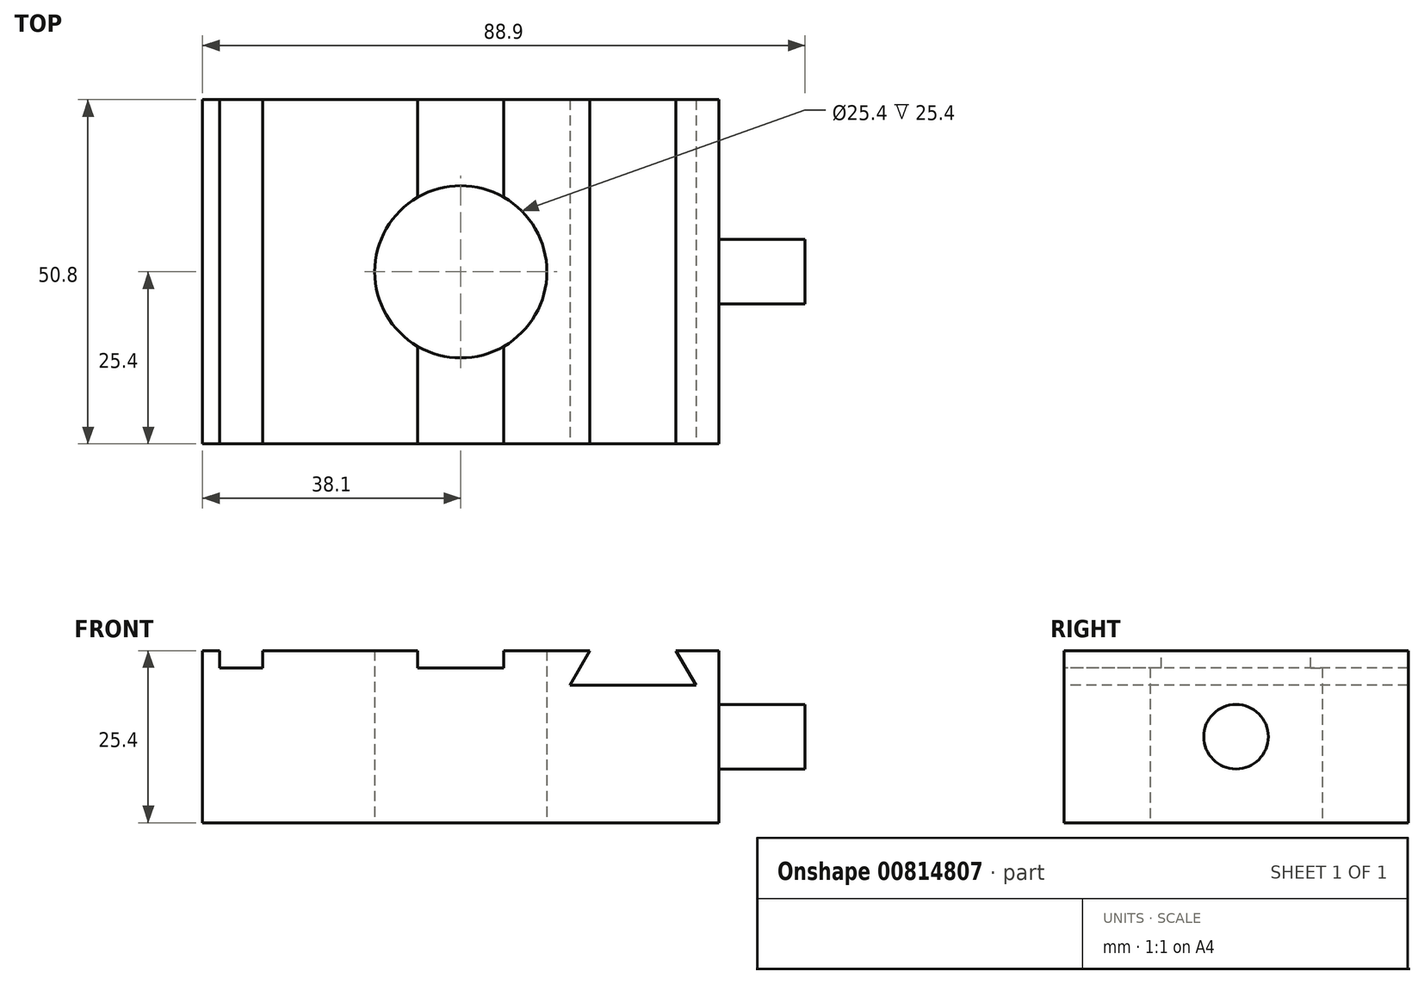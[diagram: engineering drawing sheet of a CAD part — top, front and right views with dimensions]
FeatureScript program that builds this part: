
annotation { "Feature Type Name" : "Feature", "Feature Type Description" : "" }
export const myFeature = defineFeature(function(context is Context, id is Id, definition is map)
    precondition{}
    {
        {
            var Q0;
            Q0=qCreatedBy(makeId("Top.planeOp"),FACE);
            var sketch = newSketch(context, id + "F0", { "sketchPlane" : qUnion([Q0])});
            skLineSegment(sketch, "E0.bottom", {"start": v(-38.1, 25.4) * mm, "end": v(38.1, 25.4) * mm});
            skLineSegment(sketch, "E0.top", {"start": v(-38.1, -25.4) * mm, "end": v(38.1, -25.4) * mm});
            skLineSegment(sketch, "E0.left", {"start": v(-38.1, 25.4) * mm, "end": v(-38.1, -25.4) * mm});
            skLineSegment(sketch, "E0.right", {"start": v(38.1, 25.4) * mm, "end": v(38.1, -25.4) * mm});
            skPoint(sketch, "E0.middle", {"position": v(0, 0) * mm});
            skCircle(sketch, "E1", {"center": v(0, 0) * mm, "radius": 12.7 * mm});
            skSolve(sketch);
        }
        {
            var Q0;
            Q0=makeQuery(id+"F0.imprint","IMPRINT",FACE,{"disambiguationData":[TD([[makeQuery(id+"F0.imprint","IMPRINT",EDGE,{"derivedFrom":sQuery(id+"F0.wireOp",EDGE,"E0.bottom")}),-1.0]])]});
            extrude(context, id + "F1", {"entities" : qUnion([Q0]), "depth" : 25.4 * mm, "offsetDistance" : 25 * mm});
        }
        {
            var Q0;
            Q0=makeQuery(id+"F1.opExtrude","CAP_FACE",FACE,{"disambiguationData":[OSD([sQuery(id+"F0.wireOp",EDGE,"E0.bottom"),sQuery(id+"F0.wireOp",EDGE,"E0.top"),sQuery(id+"F0.wireOp",EDGE,"E0.left"),sQuery(id+"F0.wireOp",EDGE,"E0.right"),sQuery(id+"F0.wireOp",EDGE,"E1")])],"isStart":false});
            var sketch = newSketch(context, id + "F2", { "sketchPlane" : qUnion([Q0])});
            skLineSegment(sketch, "E2.bottom", {"start": v(-35.56, 25.4) * mm, "end": v(-29.21, 25.4) * mm});
            skLineSegment(sketch, "E2.top", {"start": v(-35.56, -25.4) * mm, "end": v(-29.21, -25.4) * mm});
            skLineSegment(sketch, "E2.left", {"start": v(-35.56, 25.4) * mm, "end": v(-35.56, -25.4) * mm});
            skLineSegment(sketch, "E2.right", {"start": v(-29.21, 25.4) * mm, "end": v(-29.21, -25.4) * mm});
            skLineSegment(sketch, "E3", {"start": v(-6.35, 25.4) * mm, "end": v(-6.35, -25.4) * mm});
            skLineSegment(sketch, "E4", {"start": v(-6.35, -25.4) * mm, "end": v(6.35, -25.4) * mm});
            skLineSegment(sketch, "E5", {"start": v(6.35, -25.4) * mm, "end": v(6.35, 25.4) * mm});
            skLineSegment(sketch, "E6", {"start": v(6.35, 25.4) * mm, "end": v(-6.35, 25.4) * mm});
            skLineSegment(sketch, "E7", {"start": v(0, 25.4) * mm, "end": v(0, -25.4) * mm, "construction": true});
            skSolve(sketch);
        }
        {
            var Q0;
            Q0=makeQuery(id+"F2.imprint","IMPRINT",FACE,{"disambiguationData":[TD([[makeQuery(id+"F2.imprint","IMPRINT",EDGE,{"derivedFrom":sQuery(id+"F2.wireOp",EDGE,"E2.bottom")}),-1.0]])]});
            var Q1;
            {var subQ0=sQuery(id+"F2.wireOp",EDGE,"E4");Q1=makeQuery(id+"F2.imprint","IMPRINT",FACE,{"disambiguationData":[TD([[makeQuery(id+"F2.imprint","IMPRINT",EDGE,{"derivedFrom":subQ0}),1.0]])]});}
            var Q2;
            {var subQ0=sQuery(id+"F2.wireOp",EDGE,"E6");Q2=makeQuery(id+"F2.imprint","IMPRINT",FACE,{"disambiguationData":[TD([[makeQuery(id+"F2.imprint","IMPRINT",EDGE,{"derivedFrom":subQ0}),-1.0]])]});}
            extrude(context, id + "F3", {"entities" : qUnion([Q0, Q1, Q2]), "operationType" : NewBodyOperationType.REMOVE, "oppositeDirection" : true, "depth" : 2.54 * mm, "offsetDistance" : 25 * mm});
        }
        {
            var Q0;
            Q0=makeQuery(id+"F1.opExtrude","SWEPT_FACE",FACE,{"disambiguationData":[OSD([sQuery(id+"F0.wireOp",EDGE,"E0.top")])]});
            var sketch = newSketch(context, id + "F4", { "sketchPlane" : qUnion([Q0])});
            skLineSegment(sketch, "E8", {"start": v(19.05, 25.4) * mm, "end": v(16.12, 20.32) * mm});
            skLineSegment(sketch, "E9", {"start": v(16.12, 20.32) * mm, "end": v(34.68, 20.32) * mm});
            skLineSegment(sketch, "E10", {"start": v(34.68, 20.32) * mm, "end": v(31.75, 25.4) * mm});
            skLineSegment(sketch, "E11", {"start": v(31.75, 25.4) * mm, "end": v(19.05, 25.4) * mm});
            skLineSegment(sketch, "E12", {"start": v(25.4, 20.32) * mm, "end": v(25.4, 25.4) * mm, "construction": true});
            skSolve(sketch);
        }
        {
            var Q0;
            Q0=makeQuery(id+"F4.imprint","IMPRINT",FACE,{"disambiguationData":[TD([[makeQuery(id+"F4.imprint","IMPRINT",EDGE,{"derivedFrom":sQuery(id+"F4.wireOp",EDGE,"E8")}),1.0]])]});
            extrude(context, id + "F5", {"entities" : qUnion([Q0]), "operationType" : NewBodyOperationType.REMOVE, "endBound" : BoundingType.THROUGH_ALL, "oppositeDirection" : true, "depth" : 25 * mm, "offsetDistance" : 25 * mm});
        }
        {
            var Q0;
            Q0=makeQuery(id+"F1.opExtrude","SWEPT_FACE",FACE,{"disambiguationData":[OSD([sQuery(id+"F0.wireOp",EDGE,"E0.right")])]});
            var sketch = newSketch(context, id + "F6", { "sketchPlane" : qUnion([Q0])});
            skCircle(sketch, "E13", {"center": v(0, 12.7) * mm, "radius": 4.76 * mm});
            skPoint(sketch, "E13.centerSnap0", {"position": v(-25.4, 12.7) * mm});
            skPoint(sketch, "E13.centerSnap1", {"position": v(0, 25.4) * mm});
            skSolve(sketch);
        }
        {
            var Q0;
            Q0=makeQuery(id+"F6.imprint","IMPRINT",FACE,{"disambiguationData":[TD([[makeQuery(id+"F6.imprint","IMPRINT",EDGE,{"derivedFrom":sQuery(id+"F6.wireOp",EDGE,"E13")}),1.0]])]});
            extrude(context, id + "F7", {"entities" : qUnion([Q0]), "operationType" : NewBodyOperationType.ADD, "depth" : 12.7 * mm, "offsetDistance" : 25 * mm});
        }
    });
